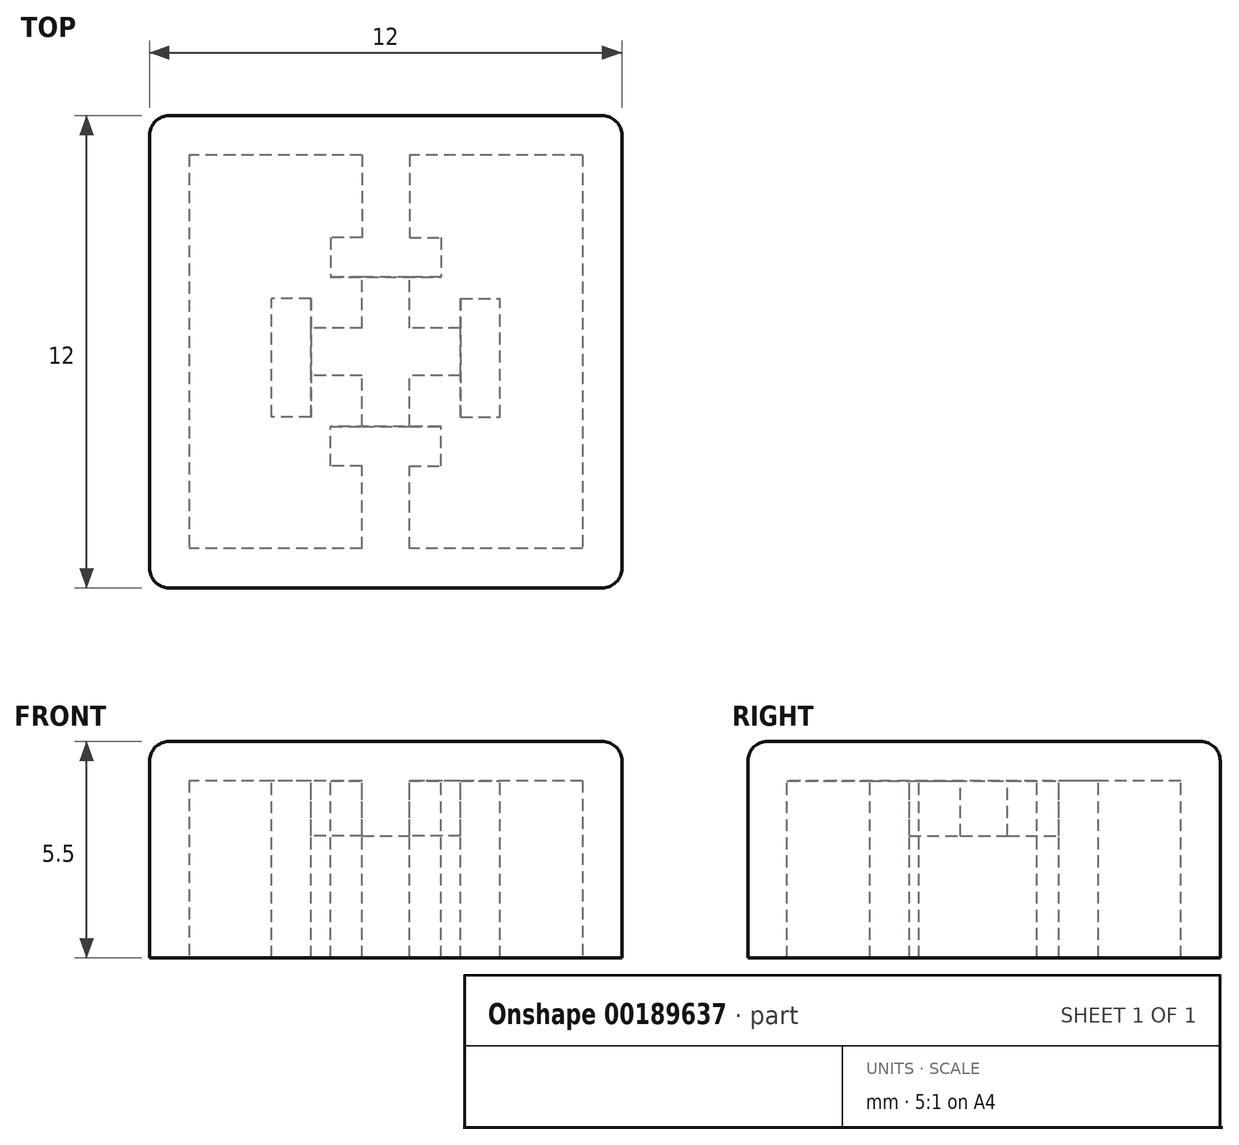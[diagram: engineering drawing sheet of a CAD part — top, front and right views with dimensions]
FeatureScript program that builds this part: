
annotation { "Feature Type Name" : "Feature", "Feature Type Description" : "" }
export const myFeature = defineFeature(function(context is Context, id is Id, definition is map)
    precondition{}
    {
        {
            var Q0;
            Q0=qCreatedBy(makeId("Top.planeOp"),FACE);
            var sketch = newSketch(context, id + "F0", { "sketchPlane" : qUnion([Q0])});
            skLineSegment(sketch, "E0.rect.bottom", {"start": v(6, 6) * mm, "end": v(-6, 6) * mm});
            skLineSegment(sketch, "E0.rect.top", {"start": v(6, -6) * mm, "end": v(-6, -6) * mm});
            skLineSegment(sketch, "E0.rect.left", {"start": v(6, 6) * mm, "end": v(6, -6) * mm});
            skLineSegment(sketch, "E0.rect.right", {"start": v(-6, 6) * mm, "end": v(-6, -6) * mm});
            skPoint(sketch, "E0.rect.middle", {"position": v(0, 0) * mm});
            skSolve(sketch);
        }
        {
            var Q0;
            Q0=qSketchRegion(id+"F0",true);
            extrude(context, id + "F1", {"entities" : qUnion([Q0]), "depth" : 5.5 * mm});
        }
        {
            var Q0;
            Q0=makeQuery(id+"F1.opExtrude","CAP_FACE",FACE,{"disambiguationData":[OSD([sQuery(id+"F0.wireOp",EDGE,"E0.rect.bottom"),sQuery(id+"F0.wireOp",EDGE,"E0.rect.top"),sQuery(id+"F0.wireOp",EDGE,"E0.rect.left"),sQuery(id+"F0.wireOp",EDGE,"E0.rect.right")])],"isStart":true});
            shell(context, id + "F2", {"entities" : qUnion([Q0]), "thickness" : 1 * mm});
        }
        {
            var Q0;
            Q0=makeQuery(id+"F2.opShell","OFFSET_FACE",FACE,{"disambiguationData":[OSD([sQuery(id+"F0.wireOp",EDGE,"E0.rect.bottom"),sQuery(id+"F0.wireOp",EDGE,"E0.rect.top"),sQuery(id+"F0.wireOp",EDGE,"E0.rect.left"),sQuery(id+"F0.wireOp",EDGE,"E0.rect.right")])]});
            var sketch = newSketch(context, id + "F3", { "sketchPlane" : qUnion([Q0])});
            skLineSegment(sketch, "E1.bottom", {"start": v(1.9, 1.65) * mm, "end": v(2.9, 1.65) * mm});
            skLineSegment(sketch, "E1.top", {"start": v(1.9, -1.35) * mm, "end": v(2.9, -1.35) * mm});
            skLineSegment(sketch, "E1.left", {"start": v(1.9, 1.65) * mm, "end": v(1.9, -1.35) * mm});
            skLineSegment(sketch, "E1.right", {"start": v(2.9, 1.65) * mm, "end": v(2.9, -1.35) * mm});
            skLineSegment(sketch, "E2", {"start": v(0.6, 5) * mm, "end": v(0.6, 2.9) * mm});
            skLineSegment(sketch, "E3", {"start": v(0.6, 2.9) * mm, "end": v(1.4, 2.9) * mm});
            skLineSegment(sketch, "E4", {"start": v(1.4, 2.9) * mm, "end": v(1.4, 1.9) * mm});
            skLineSegment(sketch, "E5", {"start": v(1.4, 1.9) * mm, "end": v(0, 1.9) * mm});
            skLineSegment(sketch, "E6", {"start": v(0, 5) * mm, "end": v(0.6, 5) * mm});
            skLineSegment(sketch, "E7", {"start": v(0, -0.76) * mm, "end": v(0, -4.07) * mm, "construction": true});
            skLineSegment(sketch, "E8.MirrorCS", {"start": v(-1.9, 1.65) * mm, "end": v(-2.9, 1.65) * mm});
            skLineSegment(sketch, "E9.MirrorCS", {"start": v(-1.9, -1.35) * mm, "end": v(-2.9, -1.35) * mm});
            skLineSegment(sketch, "E10.MirrorCS", {"start": v(-2.9, 1.65) * mm, "end": v(-2.9, -1.35) * mm});
            skLineSegment(sketch, "E11.MirrorCS", {"start": v(-1.9, 1.65) * mm, "end": v(-1.9, -1.35) * mm});
            skLineSegment(sketch, "E12", {"start": v(0, 5) * mm, "end": v(-0.6, 5) * mm});
            skLineSegment(sketch, "E13", {"start": v(-0.6, 5) * mm, "end": v(-0.6, 2.9) * mm});
            skLineSegment(sketch, "E14", {"start": v(-0.6, 2.9) * mm, "end": v(-1.4, 2.9) * mm});
            skLineSegment(sketch, "E15", {"start": v(-1.4, 2.9) * mm, "end": v(-1.4, 1.9) * mm});
            skLineSegment(sketch, "E16", {"start": v(-1.4, 1.9) * mm, "end": v(0, 1.9) * mm});
            skLineSegment(sketch, "E17", {"start": v(0.37, 0) * mm, "end": v(1.57, 0) * mm, "construction": true});
            skLineSegment(sketch, "E18.MirrorCS", {"start": v(-1.4, -1.9) * mm, "end": v(0, -1.9) * mm});
            skLineSegment(sketch, "E19.MirrorCS", {"start": v(0, -5) * mm, "end": v(0.6, -5) * mm});
            skLineSegment(sketch, "E20.MirrorCS", {"start": v(0, -5) * mm, "end": v(-0.6, -5) * mm});
            skLineSegment(sketch, "E21.MirrorCS", {"start": v(1.4, -1.9) * mm, "end": v(0, -1.9) * mm});
            skLineSegment(sketch, "E22.MirrorCS", {"start": v(0.6, -5) * mm, "end": v(0.6, -2.9) * mm});
            skLineSegment(sketch, "E23.MirrorCS", {"start": v(1.4, -2.9) * mm, "end": v(1.4, -1.9) * mm});
            skLineSegment(sketch, "E24.MirrorCS", {"start": v(0.6, -2.9) * mm, "end": v(1.4, -2.9) * mm});
            skLineSegment(sketch, "E25.MirrorCS", {"start": v(-0.6, -5) * mm, "end": v(-0.6, -2.9) * mm});
            skLineSegment(sketch, "E26.MirrorCS", {"start": v(-0.6, -2.9) * mm, "end": v(-1.4, -2.9) * mm});
            skLineSegment(sketch, "E27.MirrorCS", {"start": v(-1.4, -2.9) * mm, "end": v(-1.4, -1.9) * mm});
            skSolve(sketch);
        }
        {
            var Q0;
            Q0=qSketchRegion(id+"F3",true);
            var Q1;
            Q1=makeQuery(id+"F1.opExtrude","CAP_FACE",FACE,{"disambiguationData":[OSD([sQuery(id+"F0.wireOp",EDGE,"E0.rect.bottom"),sQuery(id+"F0.wireOp",EDGE,"E0.rect.top"),sQuery(id+"F0.wireOp",EDGE,"E0.rect.left"),sQuery(id+"F0.wireOp",EDGE,"E0.rect.right")])],"isStart":true});
            extrude(context, id + "F4", {"entities" : qUnion([Q0]), "operationType" : NewBodyOperationType.ADD, "endBound" : BoundingType.UP_TO_SURFACE, "endBoundEntityFace" : qUnion([Q1]), "depth" : 25 * mm});
        }
        {
            var Q0;
            {var subQ0=sQuery(id+"F0.wireOp",EDGE,"E0.rect.right");var subQ1=sQuery(id+"F0.wireOp",EDGE,"E0.rect.left");var subQ2=sQuery(id+"F0.wireOp",EDGE,"E0.rect.top");var subQ3=sQuery(id+"F0.wireOp",EDGE,"E0.rect.bottom");Q0=makeQuery(id+"F4.boolean.opBoolean","MERGE",FACE,{"derivedFrom":[makeQuery(id+"F1.opExtrude","CAP_FACE",FACE,{"disambiguationData":[OSD([subQ3,subQ2,subQ1,subQ0])],"isStart":true}),makeQuery(id+"F4.opExtrude","CAP_FACE",FACE,{"disambiguationData":[OSD([subQ3,subQ2,subQ1,subQ0]),ownerDisambiguation([makeQuery(id+"F4.opExtrude","SWEPT_BODY",BODY,{"disambiguationData":[OSD([sQuery(id+"F3.wireOp",EDGE,"E2"),sQuery(id+"F3.wireOp",EDGE,"E3"),sQuery(id+"F3.wireOp",EDGE,"E4"),sQuery(id+"F3.wireOp",EDGE,"E5"),sQuery(id+"F3.wireOp",EDGE,"E6"),sQuery(id+"F3.wireOp",EDGE,"E12"),sQuery(id+"F3.wireOp",EDGE,"E13"),sQuery(id+"F3.wireOp",EDGE,"E14"),sQuery(id+"F3.wireOp",EDGE,"E15"),sQuery(id+"F3.wireOp",EDGE,"E16")])]})])],"isStart":false}),makeQuery(id+"F4.opExtrude","CAP_FACE",FACE,{"disambiguationData":[OSD([subQ3,subQ2,subQ1,subQ0]),ownerDisambiguation([makeQuery(id+"F4.opExtrude","SWEPT_BODY",BODY,{"disambiguationData":[OSD([sQuery(id+"F3.wireOp",EDGE,"E18.MirrorCS"),sQuery(id+"F3.wireOp",EDGE,"E19.MirrorCS"),sQuery(id+"F3.wireOp",EDGE,"E20.MirrorCS"),sQuery(id+"F3.wireOp",EDGE,"E21.MirrorCS"),sQuery(id+"F3.wireOp",EDGE,"E22.MirrorCS"),sQuery(id+"F3.wireOp",EDGE,"E23.MirrorCS"),sQuery(id+"F3.wireOp",EDGE,"E24.MirrorCS"),sQuery(id+"F3.wireOp",EDGE,"E25.MirrorCS"),sQuery(id+"F3.wireOp",EDGE,"E26.MirrorCS"),sQuery(id+"F3.wireOp",EDGE,"E27.MirrorCS")])]})])],"isStart":false})]});}
            cPlane(context, id + "F5", {"entities" : qUnion([Q0]), "cplaneType" : CPlaneType.OFFSET, "offset" : 3.1 * mm, "oppositeDirection" : true, "width" : 150 * mm, "height" : 150 * mm});
        }
        {
            var Q0;
            Q0=makeQuery(id+"F2.opShell","OFFSET_FACE",FACE,{"disambiguationData":[OSD([sQuery(id+"F0.wireOp",EDGE,"E0.rect.bottom"),sQuery(id+"F0.wireOp",EDGE,"E0.rect.top"),sQuery(id+"F0.wireOp",EDGE,"E0.rect.left"),sQuery(id+"F0.wireOp",EDGE,"E0.rect.right")])]});
            var sketch = newSketch(context, id + "F6", { "sketchPlane" : qUnion([Q0])});
            skLineSegment(sketch, "E28.rect.bottom", {"start": v(1.9, 0.6) * mm, "end": v(-1.9, 0.6) * mm});
            skLineSegment(sketch, "E28.rect.top", {"start": v(1.9, -0.6) * mm, "end": v(-1.9, -0.6) * mm});
            skLineSegment(sketch, "E28.rect.left", {"start": v(1.9, 0.6) * mm, "end": v(1.9, -0.6) * mm});
            skLineSegment(sketch, "E28.rect.right", {"start": v(-1.9, 0.6) * mm, "end": v(-1.9, -0.6) * mm});
            skPoint(sketch, "E28.rect.middle", {"position": v(0, 0) * mm});
            skLineSegment(sketch, "E29.rect.bottom", {"start": v(0.6, 1.9) * mm, "end": v(-0.6, 1.9) * mm});
            skLineSegment(sketch, "E29.rect.top", {"start": v(0.6, -1.9) * mm, "end": v(-0.6, -1.9) * mm});
            skLineSegment(sketch, "E29.rect.left", {"start": v(0.6, 1.9) * mm, "end": v(0.6, -1.9) * mm});
            skLineSegment(sketch, "E29.rect.right", {"start": v(-0.6, 1.9) * mm, "end": v(-0.6, -1.9) * mm});
            skSolve(sketch);
        }
        {
            var Q0;
            Q0=qSketchRegion(id+"F6",true);
            var Q1;
            Q1=qCreatedBy(id+"F5.planeOp",FACE);
            extrude(context, id + "F7", {"entities" : qUnion([Q0]), "operationType" : NewBodyOperationType.ADD, "endBound" : BoundingType.UP_TO_SURFACE, "endBoundEntityFace" : qUnion([Q1]), "depth" : 25 * mm});
        }
        {
            var Q0;
            Q0=makeQuery(id+"F1.opExtrude","CAP_FACE",FACE,{"disambiguationData":[OSD([sQuery(id+"F0.wireOp",EDGE,"E0.rect.bottom"),sQuery(id+"F0.wireOp",EDGE,"E0.rect.top"),sQuery(id+"F0.wireOp",EDGE,"E0.rect.left"),sQuery(id+"F0.wireOp",EDGE,"E0.rect.right")])],"isStart":false});
            var Q1;
            Q1=makeQuery(id+"F1.opExtrude","SWEPT_EDGE",EDGE,{"disambiguationData":[OSD([sQuery(id+"F0.wireOp",EDGE,"E0.rect.bottom"),sQuery(id+"F0.wireOp",EDGE,"E0.rect.right")])]});
            var Q2;
            Q2=makeQuery(id+"F1.opExtrude","SWEPT_EDGE",EDGE,{"disambiguationData":[OSD([sQuery(id+"F0.wireOp",EDGE,"E0.rect.top"),sQuery(id+"F0.wireOp",EDGE,"E0.rect.right")])]});
            var Q3;
            Q3=makeQuery(id+"F1.opExtrude","SWEPT_EDGE",EDGE,{"disambiguationData":[OSD([sQuery(id+"F0.wireOp",EDGE,"E0.rect.top"),sQuery(id+"F0.wireOp",EDGE,"E0.rect.left")])]});
            var Q4;
            Q4=makeQuery(id+"F1.opExtrude","SWEPT_EDGE",EDGE,{"disambiguationData":[OSD([sQuery(id+"F0.wireOp",EDGE,"E0.rect.bottom"),sQuery(id+"F0.wireOp",EDGE,"E0.rect.left")])]});
            fillet(context, id + "F8", {"entities" : qUnion([Q0, Q1, Q2, Q3, Q4]), "radius" : 0.5 * mm, "tangentPropagation" : true, "allowEdgeOverflow" : false});
        }
    });
